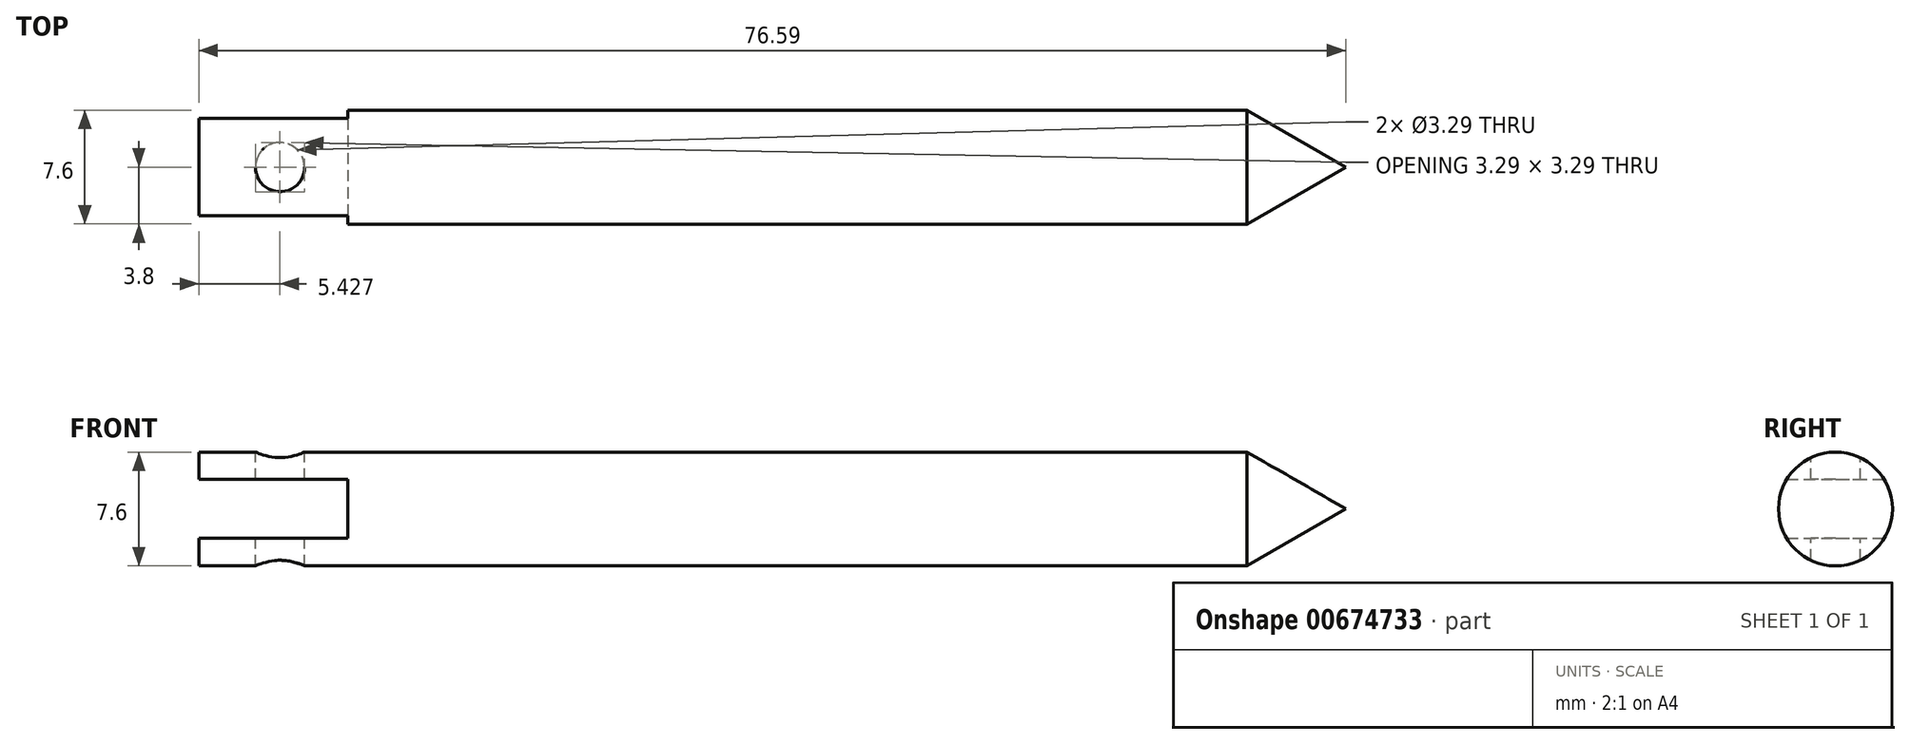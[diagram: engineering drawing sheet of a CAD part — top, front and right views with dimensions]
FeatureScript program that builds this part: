
annotation { "Feature Type Name" : "Feature", "Feature Type Description" : "" }
export const myFeature = defineFeature(function(context is Context, id is Id, definition is map)
    precondition{}
    {
        {
            var Q0;
            Q0=qCreatedBy(makeId("Front.planeOp"),FACE);
            var sketch = newSketch(context, id + "F0", { "sketchPlane" : qUnion([Q0])});
            skLineSegment(sketch, "E0", {"start": v(-52, 0) * mm, "end": v(24.58, 0) * mm});
            skLineSegment(sketch, "E1", {"start": v(24.58, 0) * mm, "end": v(18, 3.8) * mm});
            skLineSegment(sketch, "E2", {"start": v(18, 3.8) * mm, "end": v(-52, 3.8) * mm});
            skLineSegment(sketch, "E3", {"start": v(-52, 3.8) * mm, "end": v(-52, 0) * mm});
            skLineSegment(sketch, "E4.MirrorCS", {"start": v(-52, -3.8) * mm, "end": v(-52, 0) * mm});
            skLineSegment(sketch, "E5.MirrorCS", {"start": v(24.58, 0) * mm, "end": v(18, -3.8) * mm});
            skLineSegment(sketch, "E6.MirrorCS", {"start": v(18, -3.8) * mm, "end": v(-52, -3.8) * mm});
            skSolve(sketch);
        }
        {
            var Q0;
            Q0=makeQuery(id+"F0.imprint","IMPRINT",FACE,{"disambiguationData":[TD([[makeQuery(id+"F0.imprint","IMPRINT",EDGE,{"derivedFrom":sQuery(id+"F0.wireOp",EDGE,"E0")}),1.0]])]});
            var Q1;
            Q1=sQuery(id+"F0.wireOp",EDGE,"E0");
            revolve(context, id + "F1", {"entities" : qUnion([Q0]), "axis" : qUnion([Q1]), "revolveType" : RevolveType.FULL});
        }
        {
            var Q0;
            Q0=qCreatedBy(makeId("Front.planeOp"),FACE);
            var sketch = newSketch(context, id + "F2", { "sketchPlane" : qUnion([Q0])});
            skLineSegment(sketch, "E7.bottom", {"start": v(-58.37, 1.97) * mm, "end": v(-42.06, 1.97) * mm});
            skLineSegment(sketch, "E7.top", {"start": v(-58.37, -1.97) * mm, "end": v(-42.06, -1.97) * mm});
            skLineSegment(sketch, "E7.left", {"start": v(-58.37, 1.97) * mm, "end": v(-58.37, -1.97) * mm});
            skLineSegment(sketch, "E7.right", {"start": v(-42.06, 1.97) * mm, "end": v(-42.06, -1.97) * mm});
            skPoint(sketch, "E7.middle", {"position": v(-50.21, 0) * mm});
            skSolve(sketch);
        }
        {
            var Q0;
            Q0 = qSketchRegion(id + "F2", true);
            extrude(context, id + "F3", {"entities" : qUnion([Q0]), "operationType" : NewBodyOperationType.REMOVE, "endBound" : BoundingType.SYMMETRIC, "oppositeDirection" : true, "depth" : 50.8 * mm, "offsetDistance" : 25.4 * mm});
        }
        {
            var Q0;
            Q0=qCreatedBy(makeId("Top.planeOp"),FACE);
            var sketch = newSketch(context, id + "F4", { "sketchPlane" : qUnion([Q0])});
            skCircle(sketch, "E8", {"center": v(-46.58, 0) * mm, "radius": 1.65 * mm});
            skSolve(sketch);
        }
        {
            var Q0;
            Q0 = qSketchRegion(id + "F4", true);
            extrude(context, id + "F5", {"entities" : qUnion([Q0]), "operationType" : NewBodyOperationType.REMOVE, "endBound" : BoundingType.SYMMETRIC, "oppositeDirection" : true, "depth" : 50.8 * mm, "offsetDistance" : 25.4 * mm});
        }
    });
